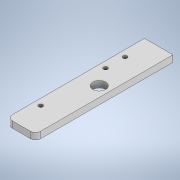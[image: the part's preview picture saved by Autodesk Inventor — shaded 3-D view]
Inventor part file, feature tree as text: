
AUTODESK INVENTOR PART (.ipt)
format: ipt  version: 2021 (Build 250183000, 183)  size: 120,832 bytes
history: native  units: mm
features: sketch x3, hole x2, extrude x1
ambient origin geometry x8: Origin, YZ Plane, XZ Plane, XY Plane, X Axis, Y Axis, Z Axis, Center Point
bodies: Solid1 (feature_tree)
feature tree (6):
  extrude  "Extrusion1"  Depth=106.0mm
  hole  "Hole1"  [1 undecoded]
  hole  "Hole2"  [1 undecoded]
  sketch  "Sketch1"  dims[d0=22.0mm d1=106.0mm]
  sketch  "Sketch2"  dims[d2=4.0mm d3=5.0mm d4=0.0mm]
  sketch  "Sketch3"  dims[d5=7.75mm d6=49.1mm d7=10.0mm d8=6.0mm d9=4.0mm d10=2.0mm d11=90.0deg d12=8.0mm d13=20.594885mm d14=17.0mm d15=20.0mm d16=35.0mm d17=85.0mm d18=3.2mm d19=6.0mm d20=4.0mm d21=2.0mm d22=90.0deg d23=8.0mm d24=20.594885mm]
note: 2 required parameter values undecoded (feature->parameter linkage not recoverable at this tier; creation-order binding heuristic only, values carry confidence <= 0.55)
